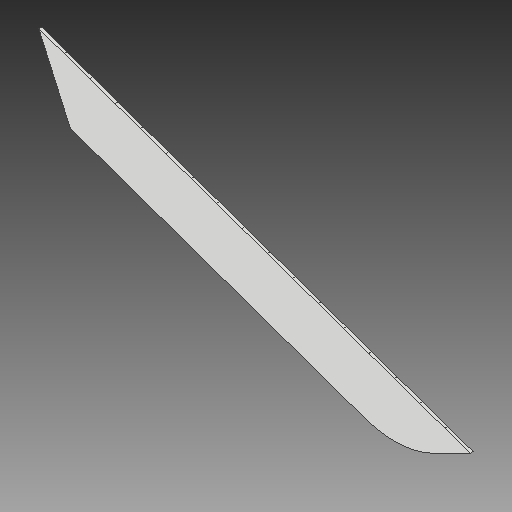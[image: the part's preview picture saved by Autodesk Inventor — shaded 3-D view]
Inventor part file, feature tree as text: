
AUTODESK INVENTOR PART (.ipt)
format: ipt  version: 2017 (Build 210142000, 142)  size: 146,944 bytes
history: native  units: in
note: dims shown in document units (in); Inventor stores cm internally (conversion verified against a paired STEP export)
features: other x3, sketch x1
ambient origin geometry x8: Origin, YZ Plane, XZ Plane, XY Plane, X Axis, Y Axis, Z Axis, Center Point
bodies: Solid1 (feature_tree)
feature tree (4):
  other  "elevon.ipt"
  other  "Solid1::elevon.ipt"
  other  "TaggingFeature1"
  sketch  "Sketch1"  dims[d0=0.3937in]
